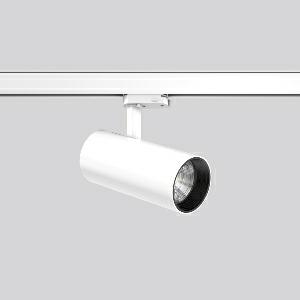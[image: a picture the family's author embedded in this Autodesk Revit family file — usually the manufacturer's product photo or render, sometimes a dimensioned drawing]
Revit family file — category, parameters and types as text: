
# Revit family: deecos_s_mini_742206_002_2_76_0d02
name_source: partatom
category: Lighting Fixtures
units: mm (PartAtom-declared; Revit-internal decimal feet)

## family parameters
Cut with Voids When Loaded = No
Host = Face
Light Source = No
Part Type = Normal
Room Calculation Point = No
Round Connector Dimension = Use Diameter
Shared = No

## types (1)
- DEECOS S mini (1 x LED Modul 927, 3000 lm, 2700)
    Apparent Load = 29 VA
    Approval mark = CE
    CIE Flux Codes = 99 100 100 100 100
    Color Rendering = 92
    Color Temperature = 2700
    Default Elevation = 1800 mm
    Description = Series: DEECOS S mini
LED surface-mounted projector in modern design with no visible cooling ribs. Housing: die-cast aluminium, powder-coated. Rotation range: 356°. Swivel range: 90°. Black plastic ring and recessed LED to prevent glare from the side. Optical assembly with lens made of plastic (polycarbonate) for the best homogeneous light distribution - can be changed without tools. Best colour rendering index Ra>90. With adapter for RZB 3-circuit DALI tracks. Suitable for Track on ceiling, Wall track. High quality converter without flickering and stroboscopic effect. The following accessories can be mounted without use of tools: interchangeable lenses, decorative glasses, honeycomb louvre, clear and frosted diffusers, white interchangeable plastic ring. 
Colour: traffic white, matt (RAL 9016)
Diameter: 87 mm
Height: 214 mm
Lamp: LED
Socket: without socket
Colour temperature: 2700K
Colour rendering index (CRI): 92
System power: 29 W
Rated luminous flux: 3000 lm
Luminous efficiency: 103 lm/W
Control gear: Converter, dimmable, DALI
Protection class: I
Type of protection: IP 20
    Height = 214 mm
    Lamp = 1 x LED Modul 927
    Lamp Light Flux = 3000 lm
    Lamp count = 1
    Length = 87 mm
    Lifetime = 50000 h
    Luminous efficacy = 103 lm/W
    Manufacturer = RZB
    ModVariant = No
    Model = 742206.002.2.76
    Mounting Place = Ceiling
    Mounting Type = Rail mounted
    Number of Poles = 1
    OnlyDefault = Yes
    Power Factor = 1
    Product Name = DEECOS S mini
    Product group = Track mounted projectors
    ProductGroupID = 301
    Protection Class = Protection class I
    Protection Degree = IP 20
    RLX_Detail_Level = 1
    RLX_Emergency_Light_Flux = 0 lm
    RLX_Emergency_Type = 0
    RLX_Emergency_Type_DB = No
    RlxData = <blob elided: 35017 chars, md5=089475f7>
    Socket = socket
    Standby Power = 0 W
    System Light Flux = 3000 lm
    System Power = 29 W
    Type Comments = Product without accessories
    Type Image = 741930.002.jpg
    URL = http://relux.com
    VarID = ---
    Voltage = 230 V
    Voltage Range = 220-240 V
    Weight = 0.00 kg
    Width = 0 mm  [stored 0 ft]

note: [stored X ft] marks values corroborated as IEEE doubles in the binary element streams (Revit-internal decimal feet)

## geometry (parser evidence)
native form markers: Blend x4, Sweep x13
no freeform markers — native parametric forms only
